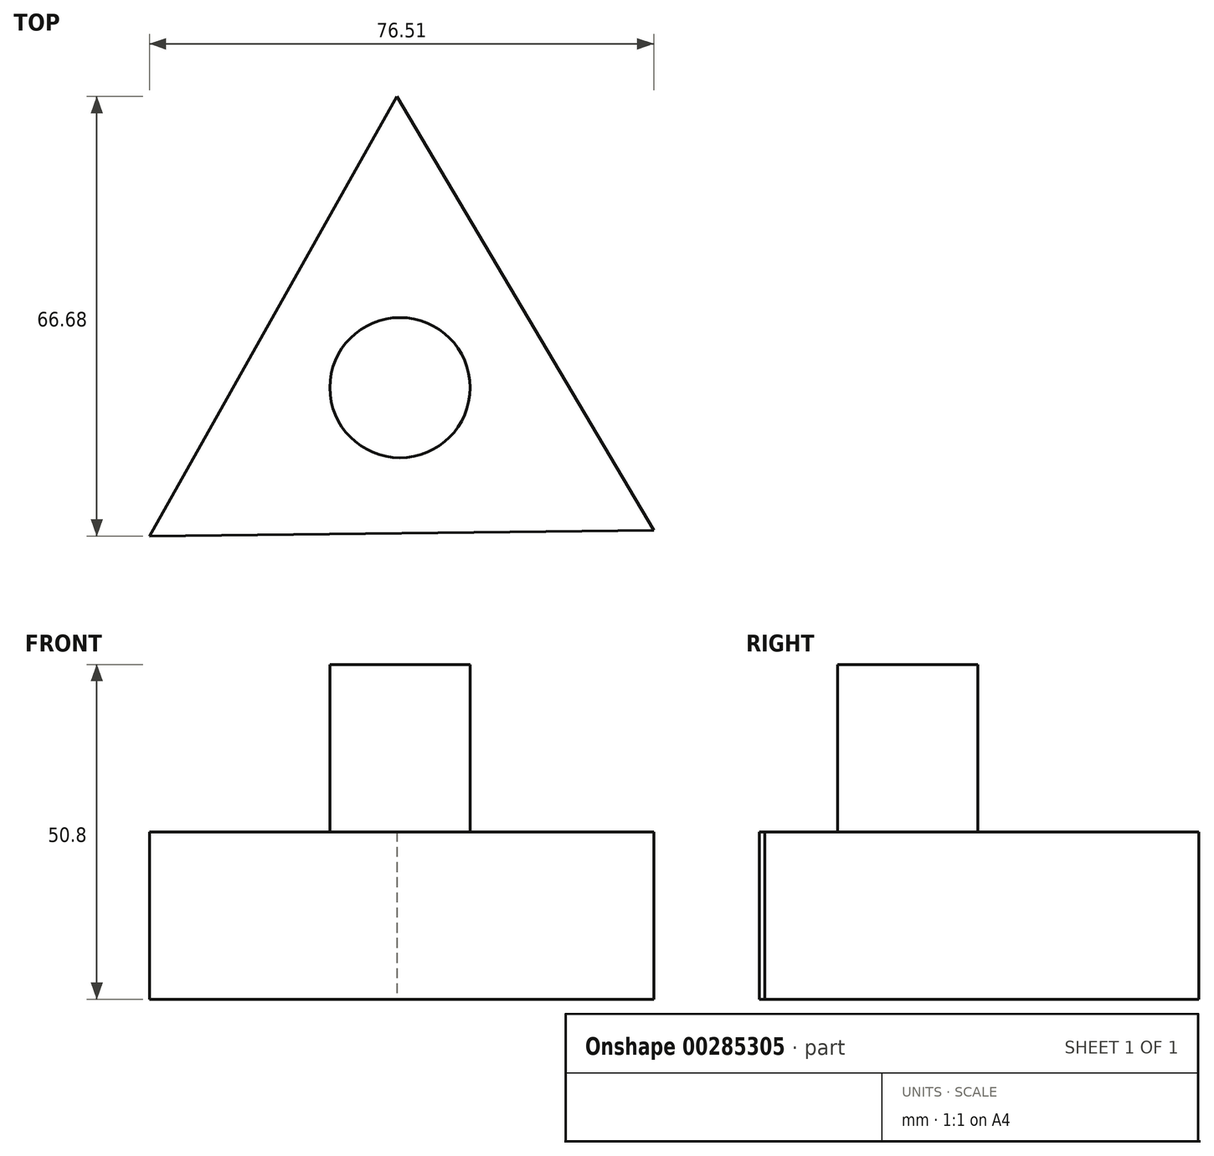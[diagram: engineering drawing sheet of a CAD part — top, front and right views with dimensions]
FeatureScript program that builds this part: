
annotation { "Feature Type Name" : "Feature", "Feature Type Description" : "" }
export const myFeature = defineFeature(function(context is Context, id is Id, definition is map)
    precondition{}
    {
        {
            var Q0;
            Q0=qCreatedBy(makeId("Top.planeOp"),FACE);
            var sketch = newSketch(context, id + "F0", { "sketchPlane" : qUnion([Q0])});
            skCircle(sketch, "E0.cCircle", {"center": v(0, 0) * mm, "radius": 22.09 * mm, "construction": true});
            skLineSegment(sketch, "E0.0", {"start": v(-38, -22.51) * mm, "end": v(-0.5, 44.17) * mm});
            skLineSegment(sketch, "E0.1", {"start": v(-0.5, 44.17) * mm, "end": v(38.5, -21.66) * mm});
            skLineSegment(sketch, "E0.2", {"start": v(38.5, -21.66) * mm, "end": v(-38, -22.51) * mm});
            skPoint(sketch, "E0.0.midPoint", {"position": v(-19.25, 10.83) * mm});
            skSolve(sketch);
        }
        {
            var Q0;
            Q0 = qSketchRegion(id + "F0", true);
            extrude(context, id + "F1", {"entities" : qUnion([Q0]), "depth" : 25.4 * mm});
        }
        {
            var Q0;
            Q0=makeQuery(id+"F1.opExtrude","CAP_FACE",FACE,{"disambiguationData":[OSD([sQuery(id+"F0.wireOp",EDGE,"E0.0"),sQuery(id+"F0.wireOp",EDGE,"E0.1"),sQuery(id+"F0.wireOp",EDGE,"E0.2")])],"isStart":false});
            var sketch = newSketch(context, id + "F2", { "sketchPlane" : qUnion([Q0])});
            skCircle(sketch, "E1", {"center": v(0, 0) * mm, "radius": 10.63 * mm});
            skSolve(sketch);
        }
        {
            var Q0;
            Q0=makeQuery(id+"F2.imprint","IMPRINT",FACE,{"disambiguationData":[TD([[makeQuery(id+"F2.imprint","IMPRINT",EDGE,{"derivedFrom":sQuery(id+"F2.wireOp",EDGE,"E1")}),1.0]])]});
            extrude(context, id + "F3", {"entities" : qUnion([Q0]), "operationType" : NewBodyOperationType.ADD, "depth" : 25.4 * mm});
        }
        {
            var Q0;
            Q0=makeQuery(id+"F3.opExtrude","CAP_FACE",FACE,{"disambiguationData":[OSD([sQuery(id+"F2.wireOp",EDGE,"E1")])],"isStart":false});
            var sketch = newSketch(context, id + "F4", { "sketchPlane" : qUnion([Q0])});
            skCircle(sketch, "E2", {"center": v(0, 0) * mm, "radius": 5.2 * mm});
            skSolve(sketch);
        }
        {
            var Q0;
            Q0=makeQuery(id+"F4.imprint","IMPRINT",FACE,{"disambiguationData":[TD([[makeQuery(id+"F4.imprint","IMPRINT",EDGE,{"derivedFrom":sQuery(id+"F4.wireOp",EDGE,"E2")}),1.0]])]});
            extrude(context, id + "F5", {"entities" : qUnion([Q0]), "operationType" : NewBodyOperationType.ADD, "oppositeDirection" : true, "depth" : 50.8 * mm});
        }
    });
